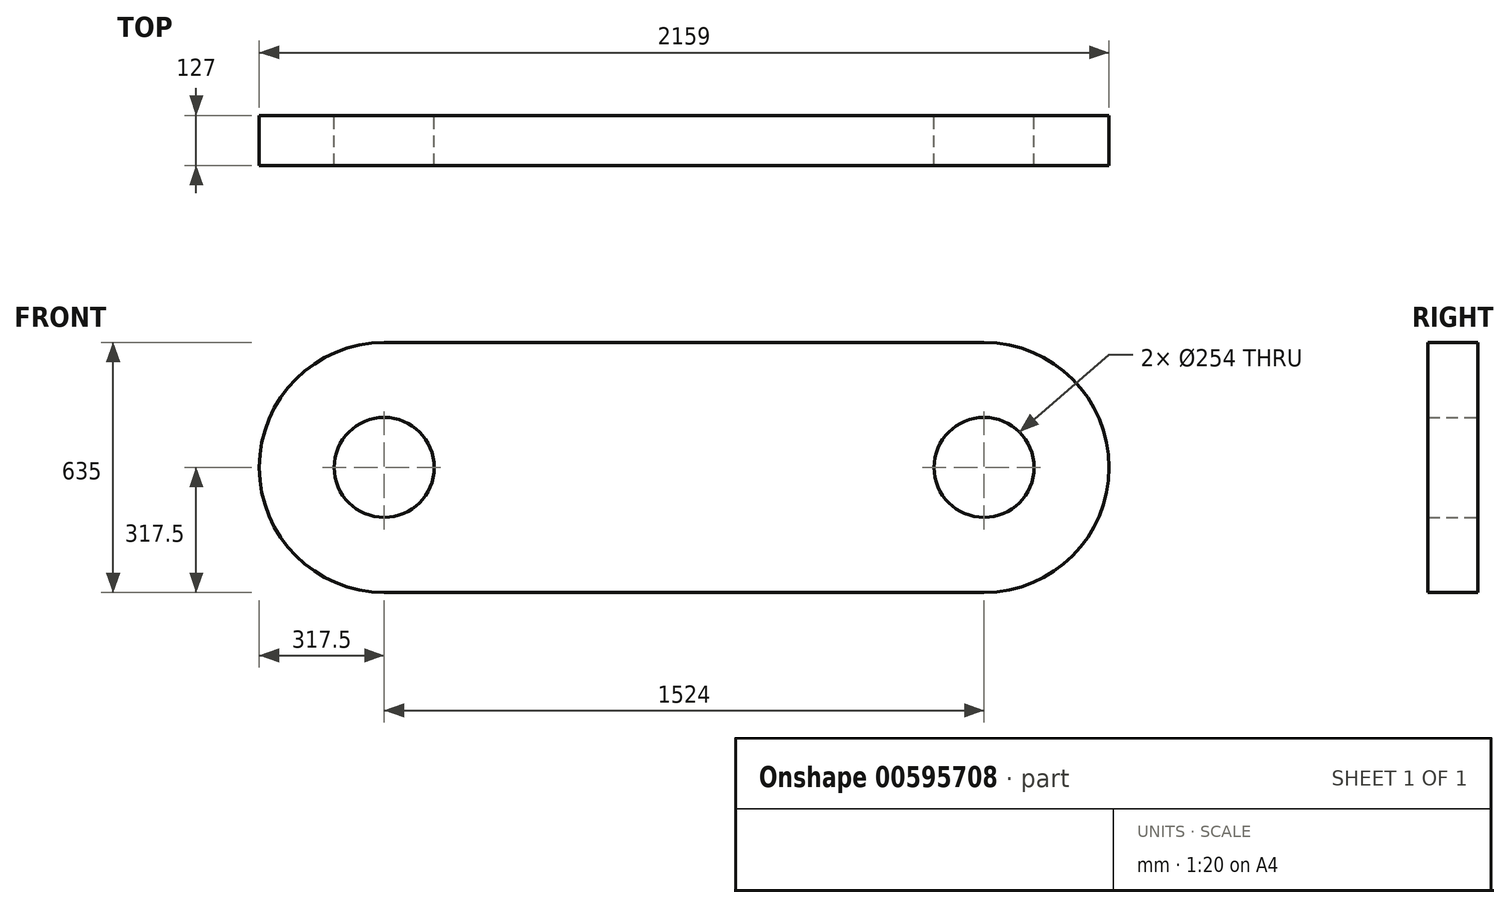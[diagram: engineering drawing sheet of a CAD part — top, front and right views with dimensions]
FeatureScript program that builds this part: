
annotation { "Feature Type Name" : "Feature", "Feature Type Description" : "" }
export const myFeature = defineFeature(function(context is Context, id is Id, definition is map)
    precondition{}
    {
        {
            var Q0;
            Q0=qCreatedBy(makeId("Front.planeOp"),FACE);
            var sketch = newSketch(context, id + "F0", { "sketchPlane" : qUnion([Q0])});
            skLineSegment(sketch, "E0.bottom", {"start": v(-762, 317.5) * mm, "end": v(762, 317.5) * mm});
            skLineSegment(sketch, "E0.top", {"start": v(-762, -317.5) * mm, "end": v(762, -317.5) * mm});
            skArc(sketch, "E1", {"start": v(762, -317.5) * mm, "mid": v(1079.5, 0) * mm, "end": v(762, 317.5) * mm});
            skArc(sketch, "E2", {"start": v(-762, 317.5) * mm, "mid": v(-1079.5, 0) * mm, "end": v(-762, -317.5) * mm});
            skCircle(sketch, "E3", {"center": v(-762, 0) * mm, "radius": 127 * mm});
            skCircle(sketch, "E4", {"center": v(762, 0) * mm, "radius": 127 * mm});
            skSolve(sketch);
        }
        {
            var Q0;
            Q0 = qSketchRegion(id + "F0", true);
            extrude(context, id + "F1", {"entities" : qUnion([Q0]), "endBound" : BoundingType.SYMMETRIC, "depth" : 127 * mm, "offsetDistance" : 25.4 * mm});
        }
    });
